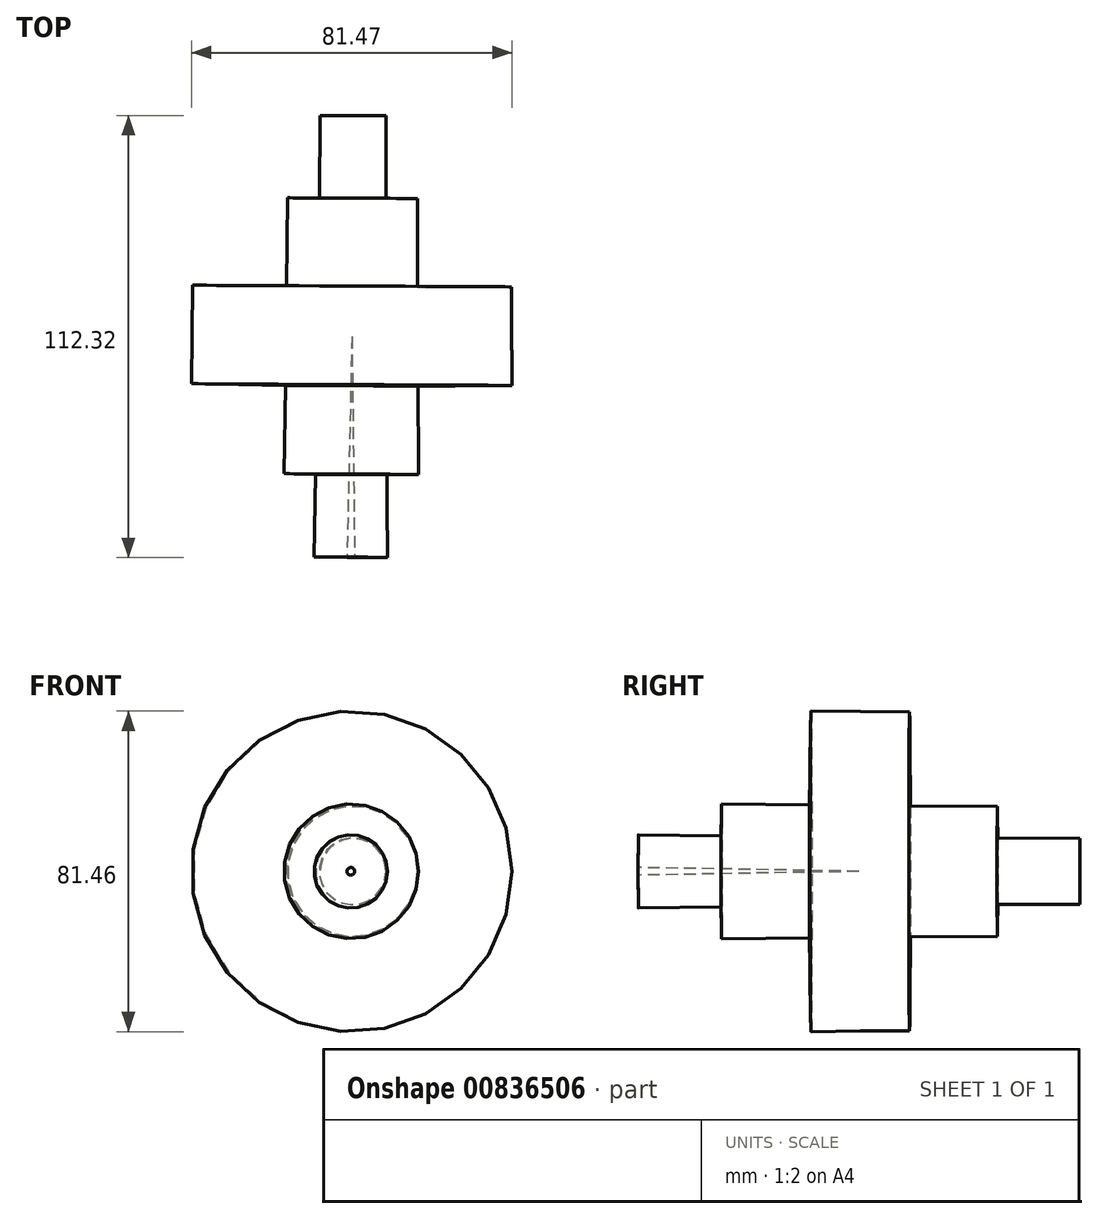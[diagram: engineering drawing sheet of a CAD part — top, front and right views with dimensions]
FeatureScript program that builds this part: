
annotation { "Feature Type Name" : "Feature", "Feature Type Description" : "" }
export const myFeature = defineFeature(function(context is Context, id is Id, definition is map)
    precondition{}
    {
        {
            var Q0;
            Q0=qCreatedBy(makeId("Top.planeOp"),FACE);
            var sketch = newSketch(context, id + "F0", { "sketchPlane" : qUnion([Q0])});
            skLineSegment(sketch, "E0", {"start": v(0, 55.98) * mm, "end": v(8.5, 55.98) * mm});
            skLineSegment(sketch, "E1", {"start": v(8.5, 55.98) * mm, "end": v(8.5, 34.97) * mm});
            skLineSegment(sketch, "E2", {"start": v(8.5, 34.97) * mm, "end": v(16.55, 34.97) * mm});
            skLineSegment(sketch, "E3", {"start": v(16.55, 34.97) * mm, "end": v(16.55, 12.52) * mm});
            skLineSegment(sketch, "E4", {"start": v(16.55, 12.52) * mm, "end": v(40.44, 12.52) * mm});
            skLineSegment(sketch, "E5", {"start": v(40.44, 12.52) * mm, "end": v(40.44, 0) * mm});
            skLineSegment(sketch, "E6", {"start": v(40.44, 0) * mm, "end": v(-0.14, -0.14) * mm, "construction": true});
            skLineSegment(sketch, "E7", {"start": v(-0.14, -0.14) * mm, "end": v(0.14, 56.27) * mm});
            skLineSegment(sketch, "E8.MirrorCS", {"start": v(40.53, -12.52) * mm, "end": v(40.44, 0) * mm});
            skLineSegment(sketch, "E9.MirrorCS", {"start": v(16.64, -12.69) * mm, "end": v(40.53, -12.52) * mm});
            skLineSegment(sketch, "E10.MirrorCS", {"start": v(8.74, -35.2) * mm, "end": v(16.8, -35.14) * mm});
            skLineSegment(sketch, "E11.MirrorCS", {"start": v(16.8, -35.14) * mm, "end": v(16.64, -12.69) * mm});
            skLineSegment(sketch, "E12.MirrorCS", {"start": v(0.4, -56.26) * mm, "end": v(8.89, -56.2) * mm});
            skLineSegment(sketch, "E13.MirrorCS", {"start": v(8.89, -56.2) * mm, "end": v(8.74, -35.2) * mm});
            skLineSegment(sketch, "E14.MirrorCS", {"start": v(-0.14, -0.14) * mm, "end": v(0.54, -56.55) * mm});
            skSolve(sketch);
        }
        {
            var Q0;
            {var subQ5=sQuery(id+"F0.wireOp",EDGE,"E1");Q0=makeQuery(id+"F0.imprint","IMPRINT",FACE,{"disambiguationData":[TD([[makeQuery(id+"F0.imprint","IMPRINT",EDGE,{"derivedFrom":subQ5}),-1.0]])]});}
            var Q1;
            Q1=sQuery(id+"F0.wireOp",EDGE,"E7");
            revolve(context, id + "F1", {"surfaceOperationType" : NewSurfaceOperationType.NEW, "entities" : qUnion([Q0]), "axis" : qUnion([Q1]), "revolveType" : RevolveType.FULL});
        }
    });
